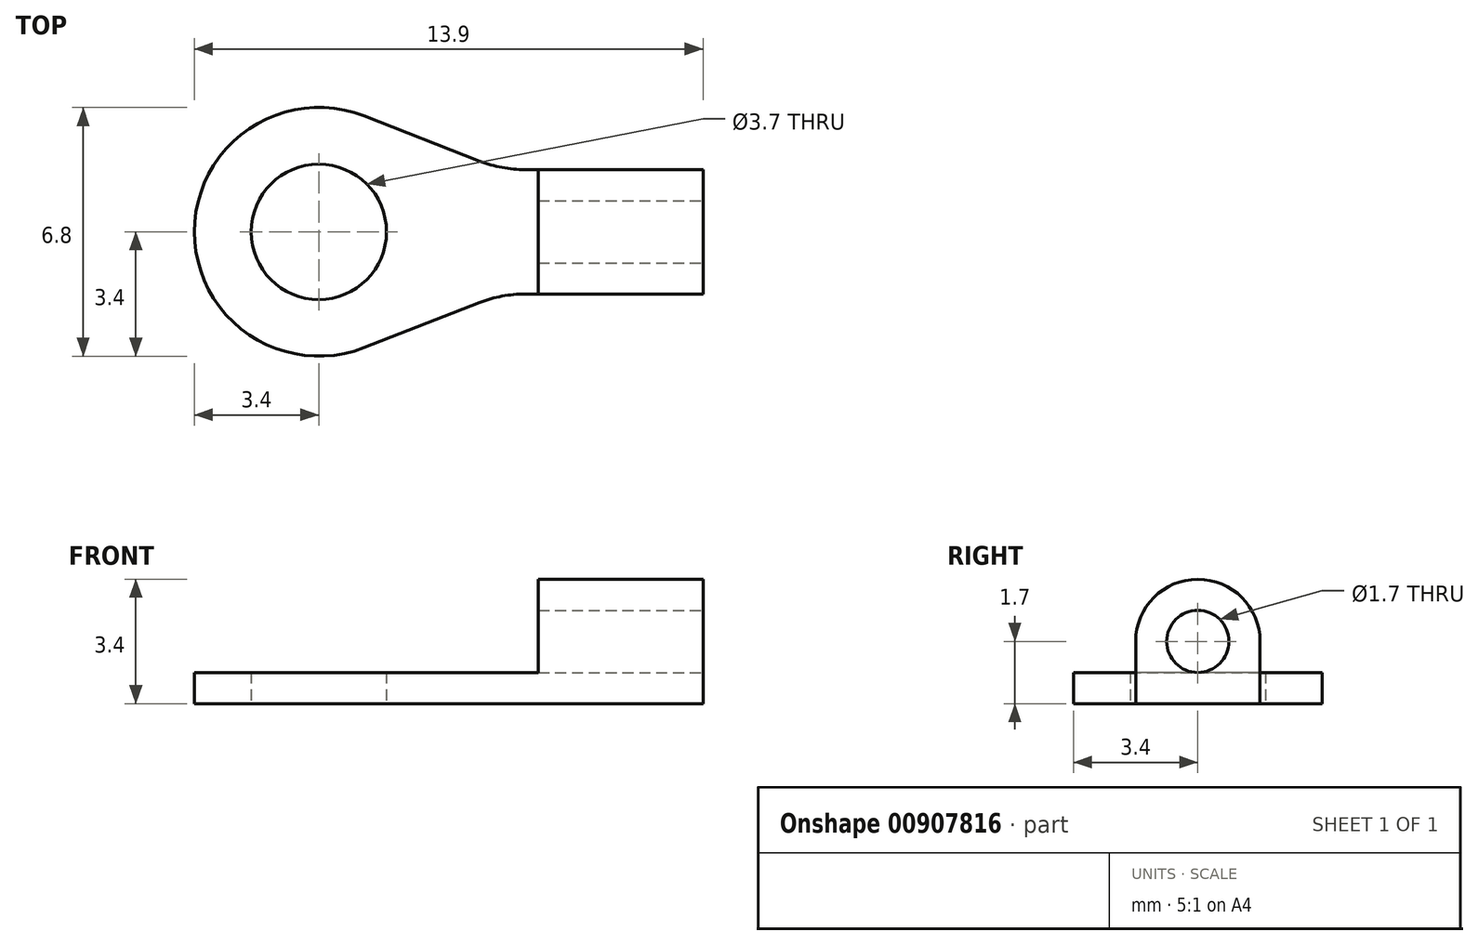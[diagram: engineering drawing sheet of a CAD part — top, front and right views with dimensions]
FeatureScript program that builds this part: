
annotation { "Feature Type Name" : "Feature", "Feature Type Description" : "" }
export const myFeature = defineFeature(function(context is Context, id is Id, definition is map)
    precondition{}
    {
        {
            var Q0;
            Q0=qCreatedBy(makeId("Top.planeOp"),FACE);
            var sketch = newSketch(context, id + "F0", { "sketchPlane" : qUnion([Q0])});
            skLineSegment(sketch, "E0.left", {"start": v(0, 3.4) * mm, "end": v(0, 3.4) * mm});
            skLineSegment(sketch, "E0.right", {"start": v(13.9, 1.7) * mm, "end": v(13.9, 5.1) * mm});
            skPoint(sketch, "E1.visualSharp", {"position": v(0, 6.8) * mm});
            skArc(sketch, "E1.filletArc", {"start": v(3.4, 6.8) * mm, "mid": v(1, 5.8) * mm, "end": v(0, 3.4) * mm});
            skPoint(sketch, "E2.visualSharp", {"position": v(0, 0) * mm});
            skArc(sketch, "E2.filletArc", {"start": v(0, 3.4) * mm, "mid": v(1, 1) * mm, "end": v(3.4, 0) * mm});
            skLineSegment(sketch, "E3.bottom", {"start": v(13.9, 1.7) * mm, "end": v(9.04, 1.7) * mm});
            skLineSegment(sketch, "E3.top", {"start": v(13.9, 5.1) * mm, "end": v(9.04, 5.1) * mm});
            skPoint(sketch, "E3.middle", {"position": v(13.9, 3.4) * mm});
            skArc(sketch, "E4", {"start": v(4.63, 6.57) * mm, "mid": v(0, 3.4) * mm, "end": v(4.63, 0.23) * mm});
            skCircle(sketch, "E5", {"center": v(3.4, 3.4) * mm, "radius": 1.85 * mm});
            skLineSegment(sketch, "E6", {"start": v(7.8, 5.33) * mm, "end": v(4.63, 6.57) * mm});
            skLineSegment(sketch, "E7", {"start": v(7.8, 1.47) * mm, "end": v(4.63, 0.23) * mm});
            skPoint(sketch, "E8.visualSharp", {"position": v(8.4, 5.1) * mm});
            skArc(sketch, "E8.filletArc", {"start": v(7.8, 5.33) * mm, "mid": v(8.41, 5.16) * mm, "end": v(9.04, 5.1) * mm});
            skPoint(sketch, "E9.visualSharp", {"position": v(8.4, 1.7) * mm});
            skArc(sketch, "E9.filletArc", {"start": v(9.04, 1.7) * mm, "mid": v(8.41, 1.64) * mm, "end": v(7.8, 1.47) * mm});
            skPoint(sketch, "E3.left.end.orphan", {"position": v(18.4, 5.1) * mm});
            skPoint(sketch, "E10.orphan", {"position": v(18.4, 1.7) * mm});
            skPoint(sketch, "E0.top.end.orphan", {"position": v(13.9, 6.8) * mm});
            skPoint(sketch, "E0.bottom.end.orphan", {"position": v(13.9, 0) * mm});
            skPoint(sketch, "E3.right.end.orphan", {"position": v(9.4, 5.1) * mm});
            skPoint(sketch, "E3.right.start.orphan", {"position": v(9.4, 1.7) * mm});
            skSolve(sketch);
        }
        {
            var Q0;
            Q0=makeQuery(id+"F0.imprint","IMPRINT",FACE,{"disambiguationData":[TD([[makeQuery(id+"F0.imprint","IMPRINT",EDGE,{"derivedFrom":sQuery(id+"F0.wireOp",EDGE,"E0.right")}),1.0]])]});
            extrude(context, id + "F1", {"entities" : qUnion([Q0]), "depth" : 0.85 * mm, "offsetDistance" : 25 * mm});
        }
        {
            var Q0;
            Q0=makeQuery(id+"F1.opExtrude","CAP_FACE",FACE,{"disambiguationData":[OSD([sQuery(id+"F0.wireOp",EDGE,"E0.right"),sQuery(id+"F0.wireOp",EDGE,"E3.bottom"),sQuery(id+"F0.wireOp",EDGE,"E3.top"),sQuery(id+"F0.wireOp",EDGE,"E4"),sQuery(id+"F0.wireOp",EDGE,"E5"),sQuery(id+"F0.wireOp",EDGE,"E6"),sQuery(id+"F0.wireOp",EDGE,"E7"),sQuery(id+"F0.wireOp",EDGE,"E8.filletArc"),sQuery(id+"F0.wireOp",EDGE,"E9.filletArc")])],"isStart":false});
            var sketch = newSketch(context, id + "F2", { "sketchPlane" : qUnion([Q0])});
            skLineSegment(sketch, "E11.bottom", {"start": v(13.9, 5.1) * mm, "end": v(9.4, 5.1) * mm});
            skLineSegment(sketch, "E11.top", {"start": v(13.9, 1.7) * mm, "end": v(9.4, 1.7) * mm});
            skLineSegment(sketch, "E11.left", {"start": v(13.9, 5.1) * mm, "end": v(13.9, 1.7) * mm});
            skLineSegment(sketch, "E11.right", {"start": v(9.4, 5.1) * mm, "end": v(9.4, 1.7) * mm});
            skSolve(sketch);
        }
        {
            var Q0;
            Q0=makeQuery(id+"F2.imprint","IMPRINT",FACE,{"disambiguationData":[TD([[makeQuery(id+"F2.imprint","IMPRINT",EDGE,{"derivedFrom":sQuery(id+"F2.wireOp",EDGE,"E11.bottom")}),1.0]])]});
            extrude(context, id + "F3", {"entities" : qUnion([Q0]), "operationType" : NewBodyOperationType.ADD, "depth" : 2.55 * mm, "offsetDistance" : 25 * mm});
        }
        {
            var Q0;
            Q0=makeQuery(id+"F3.opExtrude","CAP_EDGE",EDGE,{"disambiguationData":[OSD([sQuery(id+"F2.wireOp",EDGE,"E11.bottom")])],"isStart":false});
            var Q1;
            Q1=makeQuery(id+"F3.opExtrude","CAP_EDGE",EDGE,{"disambiguationData":[OSD([sQuery(id+"F2.wireOp",EDGE,"E11.top")])],"isStart":false});
            fillet(context, id + "F4", {"entities" : qUnion([Q0, Q1]), "radius" : 1.7 * mm, "tangentPropagation" : true, "allowEdgeOverflow" : false});
        }
        {
            var Q0;
            Q0=makeQuery(id+"F3.boolean.opBoolean","MERGE",FACE,{"derivedFrom":[makeQuery(id+"F1.opExtrude","SWEPT_FACE",FACE,{"disambiguationData":[OSD([sQuery(id+"F0.wireOp",EDGE,"E0.right")])]}),makeQuery(id+"F3.opExtrude","SWEPT_FACE",FACE,{"disambiguationData":[OSD([sQuery(id+"F2.wireOp",EDGE,"E11.left")])]})]});
            var sketch = newSketch(context, id + "F5", { "sketchPlane" : qUnion([Q0])});
            skCircle(sketch, "E12", {"center": v(3.4, 1.7) * mm, "radius": 0.85 * mm});
            skSolve(sketch);
        }
        {
            var Q0;
            Q0=makeQuery(id+"F5.imprint","IMPRINT",FACE,{"disambiguationData":[TD([[makeQuery(id+"F5.imprint","IMPRINT",EDGE,{"derivedFrom":sQuery(id+"F5.wireOp",EDGE,"E12")}),1.0]])]});
            extrude(context, id + "F6", {"entities" : qUnion([Q0]), "operationType" : NewBodyOperationType.REMOVE, "oppositeDirection" : true, "depth" : 25 * mm, "offsetDistance" : 25 * mm});
        }
    });
